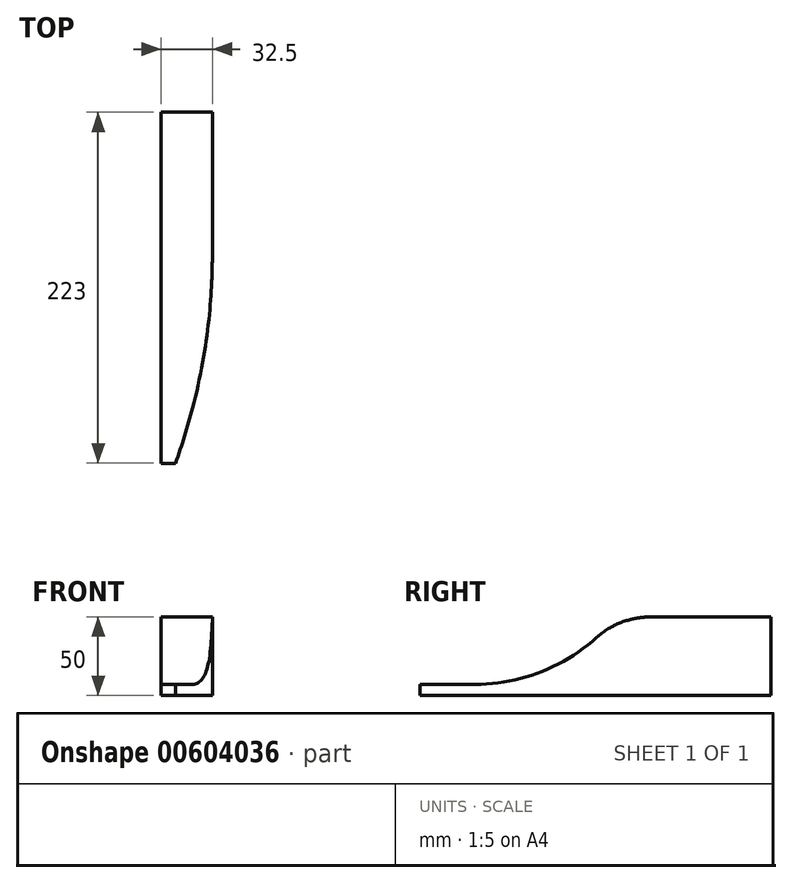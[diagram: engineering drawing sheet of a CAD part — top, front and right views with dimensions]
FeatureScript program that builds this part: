
annotation { "Feature Type Name" : "Feature", "Feature Type Description" : "" }
export const myFeature = defineFeature(function(context is Context, id is Id, definition is map)
    precondition{}
    {
        {
            var Q0;
            Q0=qCreatedBy(makeId("Top.planeOp"),FACE);
            var sketch = newSketch(context, id + "F0", { "sketchPlane" : qUnion([Q0])});
            skLineSegment(sketch, "E0", {"start": v(0, 110.26) * mm, "end": v(0, -112.74) * mm});
            skLineSegment(sketch, "E1", {"start": v(0, 110.26) * mm, "end": v(32.5, 110.26) * mm});
            skLineSegment(sketch, "E2", {"start": v(0, -112.74) * mm, "end": v(9, -112.74) * mm});
            skLineSegment(sketch, "E3", {"start": v(32.5, 110.26) * mm, "end": v(32.5, 20.26) * mm});
            skArc(sketch, "E4", {"start": v(9, -112.74) * mm, "mid": v(26.58, -47.27) * mm, "end": v(32.5, 20.26) * mm});
            skSolve(sketch);
        }
        {
            var Q0;
            Q0=makeQuery(id+"F0.imprint","IMPRINT",FACE,{"disambiguationData":[TD([[makeQuery(id+"F0.imprint","IMPRINT",EDGE,{"derivedFrom":sQuery(id+"F0.wireOp",EDGE,"E0")}),1.0]])]});
            extrude(context, id + "F1", {"entities" : qUnion([Q0]), "depth" : 50 * mm, "offsetDistance" : 25 * mm});
        }
        {
            var Q0;
            Q0=makeQuery(id+"F1.opExtrude","SWEPT_FACE",FACE,{"disambiguationData":[OSD([sQuery(id+"F0.wireOp",EDGE,"E0")])]});
            var sketch = newSketch(context, id + "F2", { "sketchPlane" : qUnion([Q0])});
            skLineSegment(sketch, "E5", {"start": v(-12.26, 50) * mm, "end": v(112.74, 50) * mm});
            skLineSegment(sketch, "E6", {"start": v(112.74, 50) * mm, "end": v(112.74, 7.09) * mm});
            skArc(sketch, "E7", {"start": v(-6.23, 43.5) * mm, "mid": v(-21.4, 48.41) * mm, "end": v(-37.26, 50) * mm});
            skLineSegment(sketch, "E8", {"start": v(-12.26, 50) * mm, "end": v(-37.26, 50) * mm});
            skLineSegment(sketch, "E9", {"start": v(112.74, 7.09) * mm, "end": v(77.74, 7.09) * mm});
            skArc(sketch, "E10", {"start": v(-6.23, 43.5) * mm, "mid": v(31.98, 16.58) * mm, "end": v(77.74, 7.09) * mm});
            skSolve(sketch);
        }
        {
            var Q0;
            Q0 = qSketchRegion(id + "F2", true);
            extrude(context, id + "F3", {"entities" : qUnion([Q0]), "operationType" : NewBodyOperationType.REMOVE, "oppositeDirection" : true, "depth" : 32.5 * mm, "offsetDistance" : 25 * mm});
        }
        {
            var Q0;
            Q0=makeQuery(id+"F3.boolean.opBoolean","COPY",EDGE,{"derivedFrom":makeQuery(id+"F3.opExtrude","SWEPT_EDGE",EDGE,{"disambiguationData":[OSD([sQuery(id+"F2.wireOp",EDGE,"E7"),sQuery(id+"F2.wireOp",EDGE,"E10")])]})});
            fillet(context, id + "F4", {"entities" : qUnion([Q0]), "radius" : 50 * mm, "tangentPropagation" : true, "allowEdgeOverflow" : false});
        }
    });
